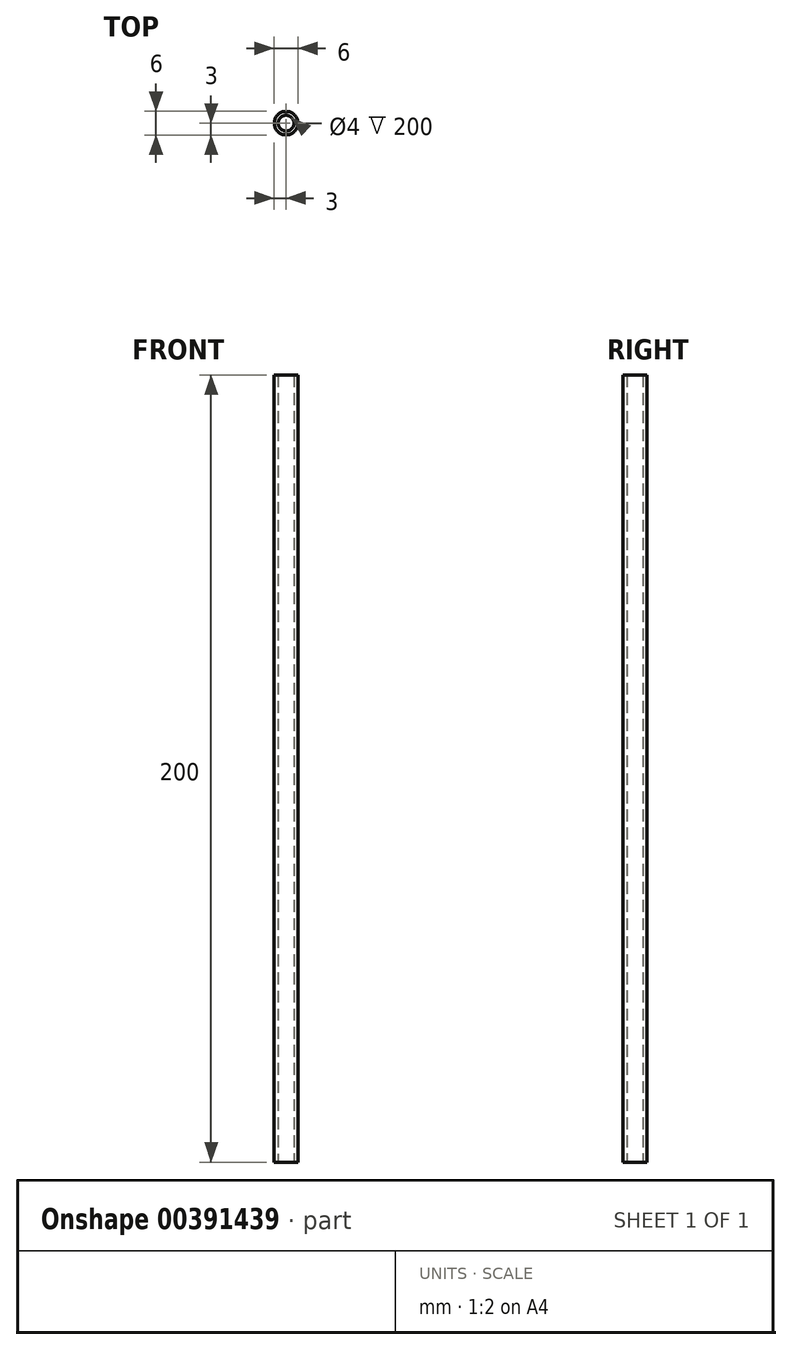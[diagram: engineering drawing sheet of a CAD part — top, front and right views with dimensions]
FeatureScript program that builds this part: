
annotation { "Feature Type Name" : "Feature", "Feature Type Description" : "" }
export const myFeature = defineFeature(function(context is Context, id is Id, definition is map)
    precondition{}
    {
        {
            var Q0;
            Q0=qCreatedBy(makeId("Front.planeOp"),FACE);
            var sketch = newSketch(context, id + "F0", { "sketchPlane" : qUnion([Q0])});
            skLineSegment(sketch, "E0", {"start": v(0, 0) * mm, "end": v(0, 200) * mm, "construction": true});
            skLineSegment(sketch, "E1.bottom", {"start": v(-3, 0) * mm, "end": v(-2, 0) * mm});
            skLineSegment(sketch, "E1.top", {"start": v(-3, 200) * mm, "end": v(-2, 200) * mm});
            skLineSegment(sketch, "E1.left", {"start": v(-3, 0) * mm, "end": v(-3, 200) * mm});
            skLineSegment(sketch, "E1.right", {"start": v(-2, 0) * mm, "end": v(-2, 200) * mm});
            skSolve(sketch);
        }
        {
            var Q0;
            Q0=qSketchRegion(id+"F0",true);
            var Q1;
            Q1=sQuery(id+"F0.wireOp",EDGE,"E0");
            revolve(context, id + "F1", {"entities" : qUnion([Q0]), "axis" : qUnion([Q1]), "revolveType" : RevolveType.FULL});
        }
    });
